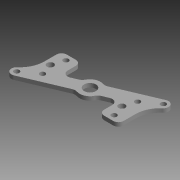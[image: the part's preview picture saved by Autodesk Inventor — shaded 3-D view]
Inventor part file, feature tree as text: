
AUTODESK INVENTOR PART (.ipt)
format: ipt  version: 2015 (Build 190159000, 159)  size: 165,376 bytes
history: native  units: mm
features: reference x7, extrude x1
ambient origin geometry x8: Origin, YZ Plane, XZ Plane, XY Plane, X Axis, Y Axis, Z Axis, Center Point
bodies: Solid1 (feature_tree)
feature tree (8):
  extrude  "Extrusion1"  Depth=4.0mm
  reference  "Reference1"
  reference  "Reference2"
  reference  "Reference3"
  reference  "Reference6"
  reference  "Reference7"
  reference  "Reference8"
  reference  "Reference9"
